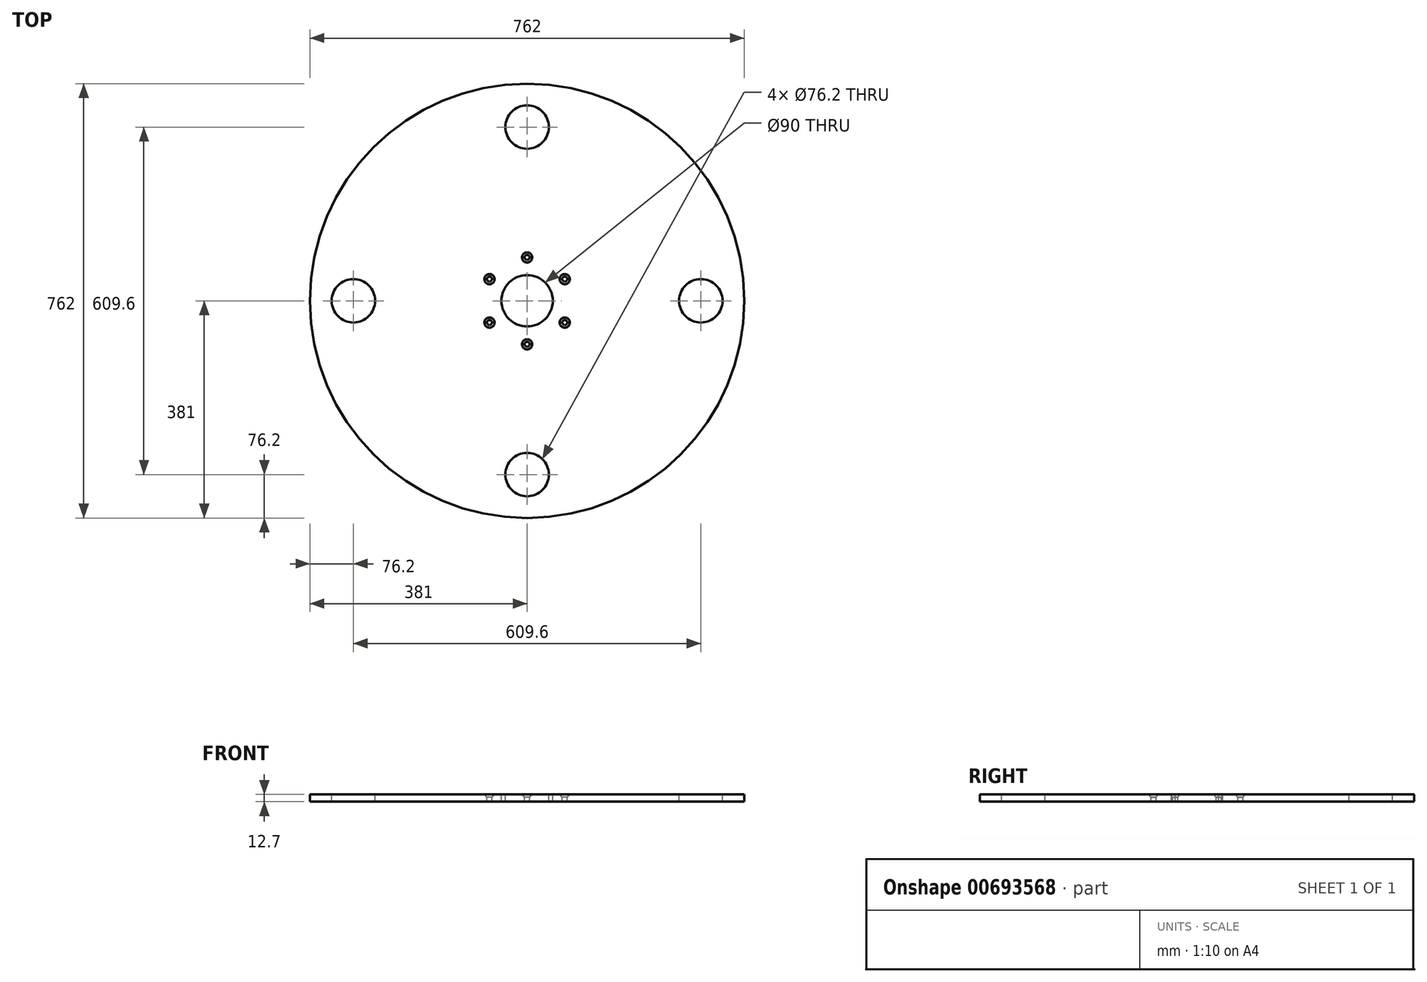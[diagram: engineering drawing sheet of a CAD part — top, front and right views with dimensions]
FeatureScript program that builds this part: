
annotation { "Feature Type Name" : "Feature", "Feature Type Description" : "" }
export const myFeature = defineFeature(function(context is Context, id is Id, definition is map)
    precondition{}
    {
        {
            var Q0;
            Q0=qCreatedBy(makeId("Top.planeOp"),FACE);
            var sketch = newSketch(context, id + "F0", { "sketchPlane" : qUnion([Q0])});
            skCircle(sketch, "E0", {"center": v(0, 0) * mm, "radius": 381 * mm});
            skSolve(sketch);
        }
        {
            var Q0;
            Q0=makeQuery(id+"F0.imprint","IMPRINT",FACE,{"disambiguationData":[TD([[makeQuery(id+"F0.imprint","IMPRINT",EDGE,{"derivedFrom":sQuery(id+"F0.wireOp",EDGE,"E0")}),1.0]])]});
            extrude(context, id + "F1", {"entities" : qUnion([Q0]), "oppositeDirection" : true, "depth" : 12.7 * mm, "offsetDistance" : 25 * mm});
        }
        {
            var Q0;
            Q0=makeQuery(id+"F1.opExtrude","CAP_FACE",FACE,{"disambiguationData":[OSD([sQuery(id+"F0.wireOp",EDGE,"E0")])],"isStart":true});
            var sketch = newSketch(context, id + "F2", { "sketchPlane" : qUnion([Q0])});
            skPoint(sketch, "E1", {"position": v(0, 0) * mm});
            skSolve(sketch);
        }
        {
            var Q0;
            Q0=sQuery(id+"F2.wireOp",VERTEX,"E1");
            var Q1;
            Q1=makeQuery(id+"F1.opExtrude","SWEPT_BODY",BODY,{"disambiguationData":[OSD([sQuery(id+"F0.wireOp",EDGE,"E0")])]});
            hole(context, id + "F3", {"style" : HoleStyle.SIMPLE, "endStyle" : HoleEndStyle.THROUGH, "holeDiameter" : 90 * mm, "majorDiameter" : 5 * mm, "isTappedThrough" : true, "tappedDepth" : 12 * mm, "tapClearance" : 3, "locations" : qUnion([Q0]), "scope" : qUnion([Q1])});
        }
        {
            var Q0;
            Q0=makeQuery(id+"F1.opExtrude","CAP_FACE",FACE,{"disambiguationData":[OSD([sQuery(id+"F0.wireOp",EDGE,"E0")])],"isStart":true});
            var sketch = newSketch(context, id + "F4", { "sketchPlane" : qUnion([Q0])});
            skCircle(sketch, "E2.cCircle", {"center": v(0, 0) * mm, "radius": 66 * mm, "construction": true});
            skLineSegment(sketch, "E2.0", {"start": v(-66, 38.1) * mm, "end": v(0, 76.2) * mm});
            skLineSegment(sketch, "E2.1", {"start": v(0, 76.2) * mm, "end": v(66, 38.1) * mm});
            skLineSegment(sketch, "E2.2", {"start": v(66, 38.1) * mm, "end": v(66, -38.1) * mm});
            skLineSegment(sketch, "E2.3", {"start": v(66, -38.1) * mm, "end": v(0, -76.2) * mm});
            skLineSegment(sketch, "E2.4", {"start": v(0, -76.2) * mm, "end": v(-66, -38.1) * mm});
            skLineSegment(sketch, "E2.5", {"start": v(-66, -38.1) * mm, "end": v(-66, 38.1) * mm});
            skPoint(sketch, "E2.0.midPoint", {"position": v(-33, 57.15) * mm});
            skSolve(sketch);
        }
        {
            var Q0;
            Q0=sQuery(id+"F4.wireOp",VERTEX,"E2.0.end");
            var Q1;
            Q1=sQuery(id+"F4.wireOp",VERTEX,"E2.2.start");
            var Q2;
            Q2=sQuery(id+"F4.wireOp",VERTEX,"E2.3.start");
            var Q3;
            Q3=sQuery(id+"F4.wireOp",VERTEX,"E2.4.start");
            var Q4;
            Q4=sQuery(id+"F4.wireOp",VERTEX,"E2.5.start");
            var Q5;
            Q5=sQuery(id+"F4.wireOp",VERTEX,"E2.5.end");
            var Q6;
            Q6=makeQuery(id+"F1.opExtrude","SWEPT_BODY",BODY,{"disambiguationData":[OSD([sQuery(id+"F0.wireOp",EDGE,"E0")])]});
            hole(context, id + "F5", {"style" : HoleStyle.C_SINK, "endStyle" : HoleEndStyle.THROUGH, "standardTappedOrClearance" : lookupTablePath({ "standard" : "ISO", "fit" : "Normal", "size" : "M8", "type" : "Clearance" }), "standardBlindInLast" : lookupTablePath({ "fit" : "Standard", "standard" : "ISO", "size" : "M8", "type" : "Clearance" }), "holeDiameter" : 8.8 * mm, "cSinkDiameter" : 17.92 * mm, "cSinkAngle" : 90 * degree, "majorDiameter" : 5 * mm, "isTappedThrough" : true, "tappedDepth" : 12 * mm, "tapClearance" : 3, "startFromSketch" : true, "locations" : qUnion([Q0, Q1, Q2, Q3, Q4, Q5]), "scope" : qUnion([Q6])});
        }
        {
            var Q0;
            Q0=makeQuery(id+"F1.opExtrude","CAP_FACE",FACE,{"disambiguationData":[OSD([sQuery(id+"F0.wireOp",EDGE,"E0")])],"isStart":true});
            var sketch = newSketch(context, id + "F6", { "sketchPlane" : qUnion([Q0])});
            skCircle(sketch, "E3.cCircle", {"center": v(0, 0) * mm, "radius": 215.53 * mm, "construction": true});
            skLineSegment(sketch, "E3.0", {"start": v(-304.8, 0) * mm, "end": v(0, 304.8) * mm, "construction": true});
            skLineSegment(sketch, "E3.1", {"start": v(0, 304.8) * mm, "end": v(304.8, 0) * mm, "construction": true});
            skLineSegment(sketch, "E3.2", {"start": v(304.8, 0) * mm, "end": v(0, -304.8) * mm, "construction": true});
            skLineSegment(sketch, "E3.3", {"start": v(0, -304.8) * mm, "end": v(-304.8, 0) * mm, "construction": true});
            skPoint(sketch, "E3.0.midPoint", {"position": v(-152.4, 152.4) * mm});
            skSolve(sketch);
        }
        {
            var Q0;
            Q0=sQuery(id+"F6.wireOp",VERTEX,"E3.1.start");
            var Q1;
            Q1=sQuery(id+"F6.wireOp",VERTEX,"E3.2.start");
            var Q2;
            Q2=sQuery(id+"F6.wireOp",VERTEX,"E3.2.end");
            var Q3;
            Q3=sQuery(id+"F6.wireOp",VERTEX,"E3.3.end");
            var Q4;
            Q4=makeQuery(id+"F1.opExtrude","SWEPT_BODY",BODY,{"disambiguationData":[OSD([sQuery(id+"F0.wireOp",EDGE,"E0")])]});
            hole(context, id + "F7", {"style" : HoleStyle.SIMPLE, "endStyle" : HoleEndStyle.THROUGH, "holeDiameter" : 76.2 * mm, "majorDiameter" : 5 * mm, "isTappedThrough" : true, "tappedDepth" : 12 * mm, "tapClearance" : 3, "startFromSketch" : true, "locations" : qUnion([Q0, Q1, Q2, Q3]), "scope" : qUnion([Q4])});
        }
    });
